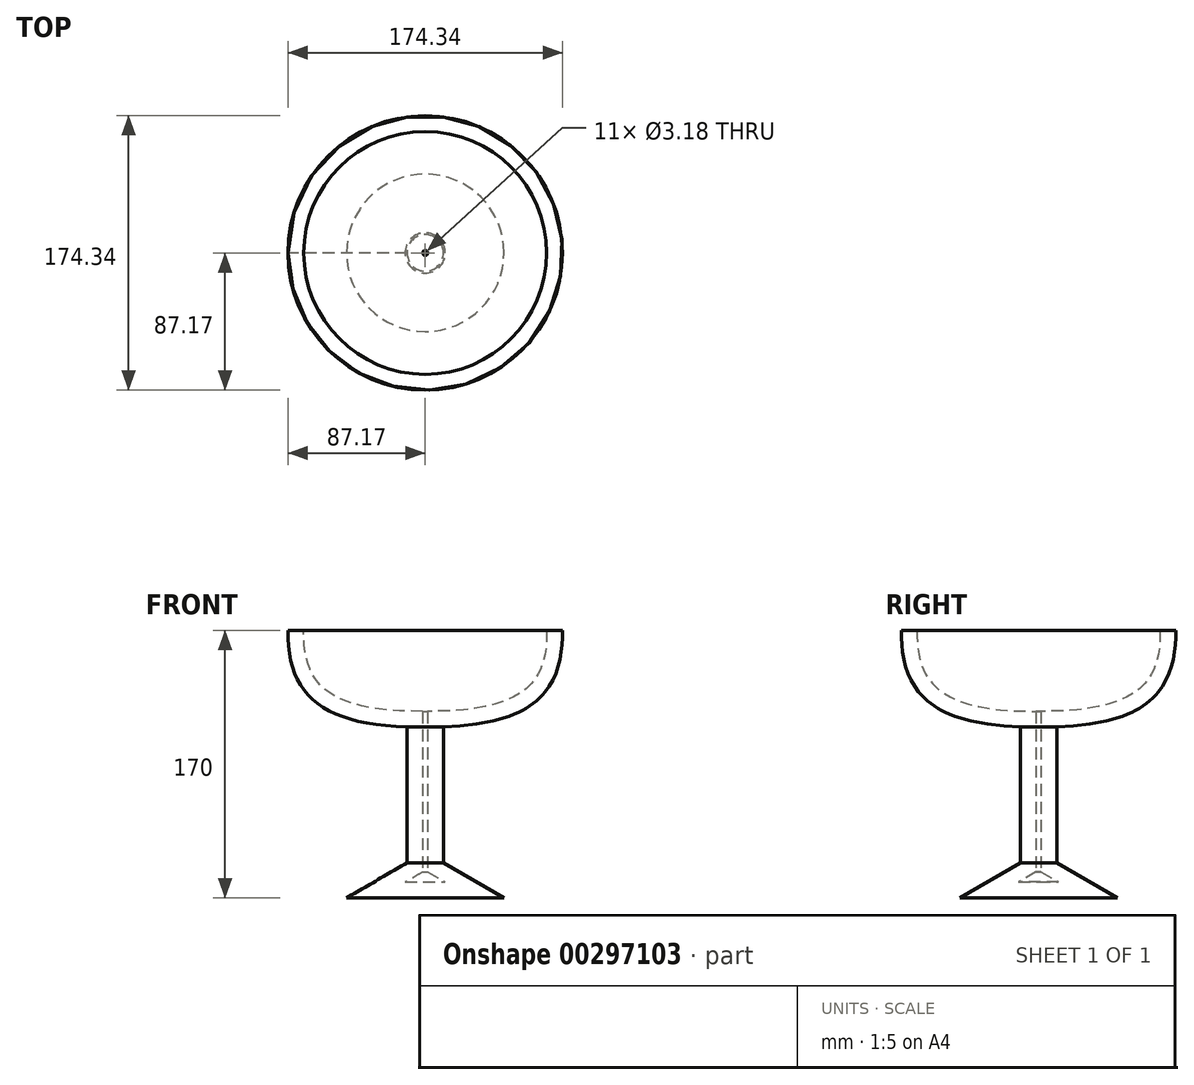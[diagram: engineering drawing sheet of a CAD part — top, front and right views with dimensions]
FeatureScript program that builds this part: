
annotation { "Feature Type Name" : "Feature", "Feature Type Description" : "" }
export const myFeature = defineFeature(function(context is Context, id is Id, definition is map)
    precondition{}
    {
        {
            var Q0;
            Q0=qCreatedBy(makeId("Front.planeOp"),FACE);
            var sketch = newSketch(context, id + "F0", { "sketchPlane" : qUnion([Q0])});
            skLineSegment(sketch, "E0", {"start": v(0, 0) * mm, "end": v(0, 170) * mm});
            skLineSegment(sketch, "E1", {"start": v(0, 0) * mm, "end": v(50, 0) * mm});
            skLineSegment(sketch, "E2", {"start": v(50, 0) * mm, "end": v(11.6, 22.2) * mm});
            skLineSegment(sketch, "E3", {"start": v(11.6, 22.2) * mm, "end": v(11.6, 108.67) * mm});
            skLineSegment(sketch, "E4", {"start": v(0, 170) * mm, "end": v(87.15, 170) * mm});
            skFitSpline(sketch, "E5", {"points": [v(11.6, 108.67) * mm, v(87.15, 170) * mm], "startDerivative": vector(163.48, 4.36) * mm, "endDerivative": vector(-2.18, 120.78) * mm});
            skSolve(sketch);
        }
        {
            var Q0;
            Q0=makeQuery(id+"F0.imprint","IMPRINT",FACE,{"disambiguationData":[TD([[makeQuery(id+"F0.imprint","IMPRINT",EDGE,{"derivedFrom":sQuery(id+"F0.wireOp",EDGE,"E0")}),-1.0]])]});
            var Q1;
            Q1=sQuery(id+"F0.wireOp",EDGE,"E0");
            revolve(context, id + "F1", {"entities" : qUnion([Q0]), "axis" : qUnion([Q1]), "revolveType" : RevolveType.FULL});
        }
        {
            var Q0;
            Q0=makeQuery(id+"F1.opRevolve","SWEPT_FACE",FACE,{"disambiguationData":[OSD([sQuery(id+"F0.wireOp",EDGE,"E4")])]});
            shell(context, id + "F2", {"entities" : qUnion([Q0]), "thickness" : 10 * mm});
        }
    });
